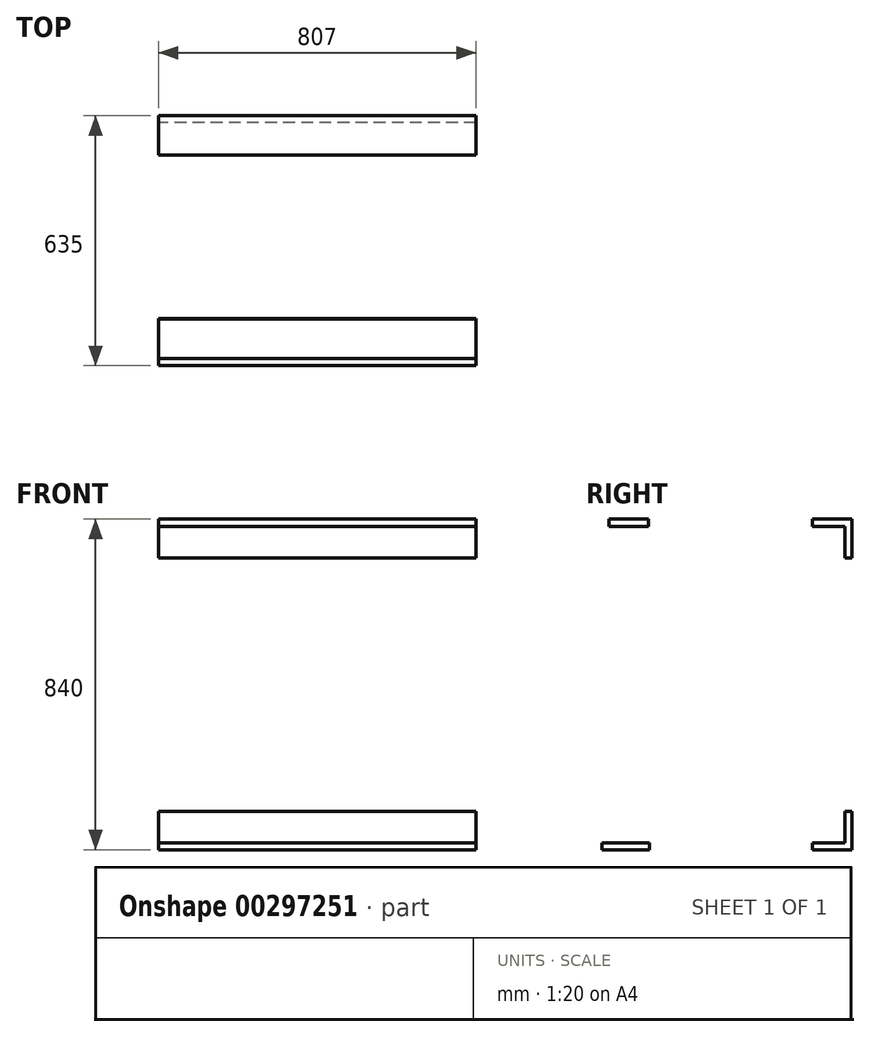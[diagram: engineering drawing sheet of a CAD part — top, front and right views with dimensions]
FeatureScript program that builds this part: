
annotation { "Feature Type Name" : "Feature", "Feature Type Description" : "" }
export const myFeature = defineFeature(function(context is Context, id is Id, definition is map)
    precondition{}
    {
        {
            var Q0;
            Q0=qCreatedBy(makeId("Right.planeOp"),FACE);
            var sketch = newSketch(context, id + "F0", { "sketchPlane" : qUnion([Q0])});
            skLineSegment(sketch, "E0.bottom", {"start": v(317.5, 420) * mm, "end": v(-317.5, 420) * mm, "construction": true});
            skLineSegment(sketch, "E0.top", {"start": v(317.5, -420) * mm, "end": v(-317.5, -420) * mm, "construction": true});
            skLineSegment(sketch, "E0.left", {"start": v(317.5, 420) * mm, "end": v(317.5, -420) * mm, "construction": true});
            skLineSegment(sketch, "E0.right", {"start": v(-317.5, 420) * mm, "end": v(-317.5, -420) * mm, "construction": true});
            skPoint(sketch, "E0.middle", {"position": v(0, 0) * mm});
            skLineSegment(sketch, "E1.bottom", {"start": v(317.5, 420) * mm, "end": v(217.5, 420) * mm});
            skLineSegment(sketch, "E1.top", {"start": v(317.5, 402) * mm, "end": v(217.5, 402) * mm});
            skLineSegment(sketch, "E1.left", {"start": v(317.5, 420) * mm, "end": v(317.5, 402) * mm});
            skLineSegment(sketch, "E1.right", {"start": v(217.5, 420) * mm, "end": v(217.5, 402) * mm});
            skLineSegment(sketch, "E2.bottom", {"start": v(317.5, 402) * mm, "end": v(299.5, 402) * mm});
            skLineSegment(sketch, "E2.top", {"start": v(317.5, 322) * mm, "end": v(299.5, 322) * mm});
            skLineSegment(sketch, "E2.left", {"start": v(317.5, 402) * mm, "end": v(317.5, 322) * mm});
            skLineSegment(sketch, "E2.right", {"start": v(299.5, 402) * mm, "end": v(299.5, 322) * mm});
            skLineSegment(sketch, "E3.bottom", {"start": v(-299.5, 420) * mm, "end": v(-199.5, 420) * mm});
            skLineSegment(sketch, "E3.top", {"start": v(-299.5, 402) * mm, "end": v(-199.5, 402) * mm});
            skLineSegment(sketch, "E3.left", {"start": v(-299.5, 420) * mm, "end": v(-299.5, 402) * mm});
            skLineSegment(sketch, "E3.right", {"start": v(-199.5, 420) * mm, "end": v(-199.5, 402) * mm});
            skLineSegment(sketch, "E4.bottom", {"start": v(-317.5, -420) * mm, "end": v(-197.5, -420) * mm});
            skLineSegment(sketch, "E4.top", {"start": v(-317.5, -402) * mm, "end": v(-197.5, -402) * mm});
            skLineSegment(sketch, "E4.left", {"start": v(-317.5, -420) * mm, "end": v(-317.5, -402) * mm});
            skLineSegment(sketch, "E4.right", {"start": v(-197.5, -420) * mm, "end": v(-197.5, -402) * mm});
            skLineSegment(sketch, "E5.bottom", {"start": v(317.5, -420) * mm, "end": v(217.5, -420) * mm});
            skLineSegment(sketch, "E5.top", {"start": v(317.5, -402) * mm, "end": v(217.5, -402) * mm});
            skLineSegment(sketch, "E5.left", {"start": v(317.5, -420) * mm, "end": v(317.5, -402) * mm});
            skLineSegment(sketch, "E5.right", {"start": v(217.5, -420) * mm, "end": v(217.5, -402) * mm});
            skLineSegment(sketch, "E6.bottom", {"start": v(317.5, -402) * mm, "end": v(299.5, -402) * mm});
            skLineSegment(sketch, "E6.top", {"start": v(317.5, -322) * mm, "end": v(299.5, -322) * mm});
            skLineSegment(sketch, "E6.left", {"start": v(317.5, -402) * mm, "end": v(317.5, -322) * mm});
            skLineSegment(sketch, "E6.right", {"start": v(299.5, -402) * mm, "end": v(299.5, -322) * mm});
            skSolve(sketch);
        }
        {
            var Q0;
            Q0=qSketchRegion(id+"F0",true);
            extrude(context, id + "F1", {"entities" : qUnion([Q0]), "depth" : 807 * mm});
        }
    });
